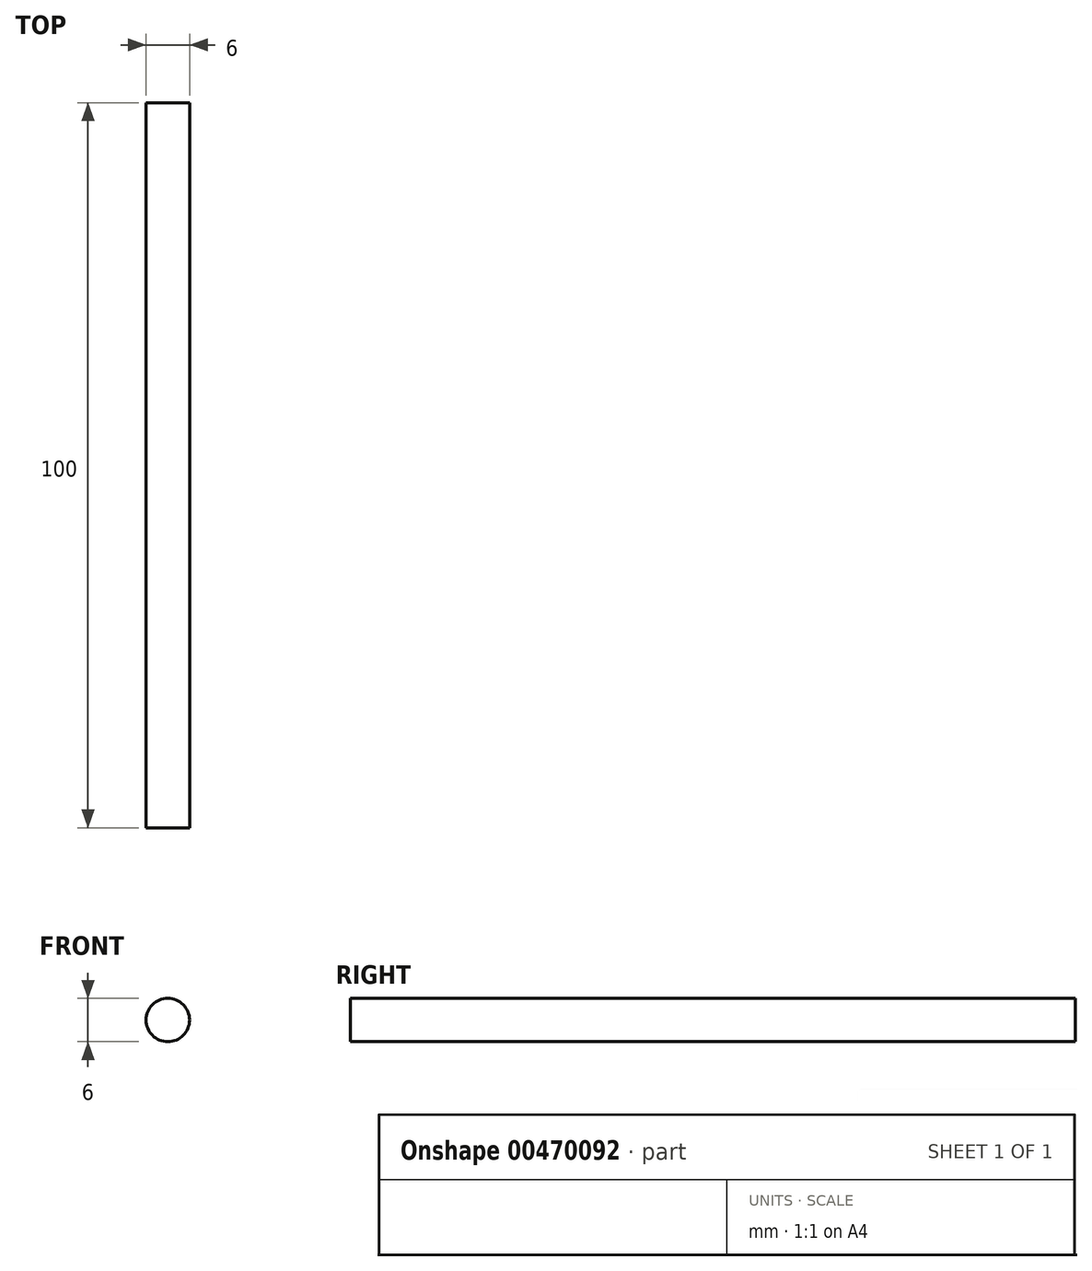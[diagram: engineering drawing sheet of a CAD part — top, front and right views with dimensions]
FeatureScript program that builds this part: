
annotation { "Feature Type Name" : "Feature", "Feature Type Description" : "" }
export const myFeature = defineFeature(function(context is Context, id is Id, definition is map)
    precondition{}
    {
        {
            var Q0;
            Q0=qCreatedBy(makeId("Front.planeOp"),FACE);
            var sketch = newSketch(context, id + "F0", { "sketchPlane" : qUnion([Q0])});
            skCircle(sketch, "E0", {"center": v(0, 0) * mm, "radius": 3 * mm});
            skSolve(sketch);
        }
        {
            var Q0;
            Q0=makeQuery(id+"F0.imprint","IMPRINT",FACE,{"disambiguationData":[TD([[makeQuery(id+"F0.imprint","IMPRINT",EDGE,{"derivedFrom":sQuery(id+"F0.wireOp",EDGE,"E0")}),1.0]])]});
            extrude(context, id + "F1", {"entities" : qUnion([Q0]), "depth" : 100 * mm});
        }
    });
